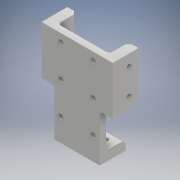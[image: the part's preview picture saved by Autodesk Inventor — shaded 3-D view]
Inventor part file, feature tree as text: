
AUTODESK INVENTOR PART (.ipt)
format: ipt  version: 2017 (Build 210142000, 142)  size: 195,072 bytes
history: native  units: mm
features: sketch x7, extrude x4, hole x3, fillet x2, chamfer x1
ambient origin geometry x8: Origin, YZ Plane, XZ Plane, XY Plane, X Axis, Y Axis, Z Axis, Center Point
bodies: Solid1 (feature_tree)
feature tree (17):
  extrude  "Extrusion1"  Depth=30.0mm
  hole  "Hole1"  [1 undecoded]
  extrude  "Extrusion2"  Depth=8.0mm
  extrude  "Extrusion3"  Depth=2.0mm
  extrude  "Extrusion5"  Depth=6.0mm
  hole  "Hole3"  [1 undecoded]
  hole  "Hole2"  [1 undecoded]
  chamfer  "Chamfer1"  Distance=10.0mm
  fillet  "Fillet2"  Radius=2.0mm
  fillet  "Fillet3"  Radius=29.0mm
  sketch  "Sketch1"  dims[d0=44.0mm d1=30.0mm]
  sketch  "Sketch2"  dims[d2=16.0mm d3=0.0mm d4=10.0mm]
  sketch  "Sketch3"  dims[d5=16.0mm d6=8.0mm]
  sketch  "Sketch4"  dims[d7=2.8mm d8=6.0mm d9=4.0mm d10=2.0mm d11=90.0deg d12=8.0mm d13=20.594885mm d14=4.0mm]
  sketch  "Sketch5"  dims[d15=6.0mm d16=6.0mm]
  sketch  "Sketch7"  dims[d17=16.0mm d18=0.0mm d19=10.0mm]
  sketch  "Sketch8"  dims[d20=10.0mm d21=20.0mm d22=10.0mm d23=3.2mm d24=6.0mm d25=4.0mm d26=2.0mm d27=90.0deg d28=8.0mm d29=20.594885mm d31=2.0mm d32=2.0mm d33=45.0deg d34=29.0mm d35=14.0mm d36=14.0mm d37=16.0mm d38=0.0mm d42=6.0mm d43=16.0mm d44=0.0mm d45=2.0mm d46=10.0mm d47=16.0mm d48=8.0mm d49=2.8mm d50=6.0mm d51=4.0mm d52=2.0mm d53=90.0deg d54=8.0mm d55=20.594885mm d56=20.0mm d57=2.0mm]
note: 3 required parameter values undecoded (feature->parameter linkage not recoverable at this tier; creation-order binding heuristic only, values carry confidence <= 0.55)
